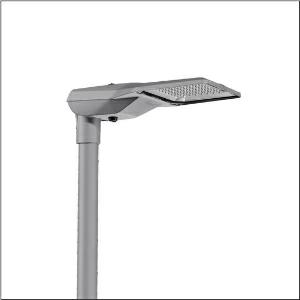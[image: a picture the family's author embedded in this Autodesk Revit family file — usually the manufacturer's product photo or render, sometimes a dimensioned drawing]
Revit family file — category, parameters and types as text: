
# Revit family: streetlight_sl_21_iq_midi___st0_8a_5xe3c31y08mb_7afc
name_source: partatom
category: Lighting Fixtures
units: mm (PartAtom-declared; Revit-internal decimal feet)

## family parameters
Cut with Voids When Loaded = No
Host = Face
Light Source = No
Part Type = Normal
Room Calculation Point = No
Round Connector Dimension = Use Diameter
Shared = No

## types (1)
- --- (1 x LED, 18340 lm, 129.3 W, 3000K)
    Apparent Load = 129 VA
    CIE Flux Codes = 38 75 97 100 100
    Color Rendering = 70
    Color Temperature = 3000K
    Default Elevation = 1800 mm
    Description = Streetlight SL 21 iQ midi, mast luminaire, primary light control with lens, of PMMA, primary optical cover: cover, of toughened safety glass, transparent, light distribution: ST0.8a, light emission: direct distribution, primary light characteristic: asymmetric, installation type: post-top, side-entry, LED, High Power LED, rated luminous flux: 18.340lm, luminous efficacy: 142lm/W, light colour: 730, colour temperature: 3000K, control: presetting dimming logarithmic, Street-Remote, Auto-Match, Temp-Guard, Lumen-Switch, Night-Set, Smart-Wire, Light-Fading, Desk-Remote (wireless, voltage-free reading and setting of iQ features in the workshop via application-optimized NFC function/RFID function), optimised constant luminous flux control (CLO 2.0), mains connection: 230..240V, AC, 50/60Hz, start of lifetime: 129W, end of service life: 142W, reduction: 56W, luminaire housing, of diecast aluminium, powder-coated, Siteco® metallic grey (DB 702S), corrosivity category C5 mid according to DIN EN ISO 12944, please order mast flange separately, inclination adjustable: 0°, 5°, 10°, 15°, sealing non-destructively replaceable, multi-level sealing system, length: 644mm, width: 335mm, height: 110mm, mast flange for spigot size: 42mm (side-entry): 5XC10008XM4, 60/48mm (side-entry/post-top): 5XC10108XM2, 76/60mm (side-entry/post-top): 5XC10108XM1, Smart Interface below and above, protection rating (complete): IP66, insulation class (complete): insulation class II (safety insulation), certification: CE, ENEC, ENEC+, VDE, impact resistance: IK09, permissible operating ambient temperature for outdoor applications: -40..+50°C, standard-compliant lighting for roads and squares, packaging unit: 1 piece

Light Distribution: ST0.8a
    Height = 111 mm
    Lamp = 1 x LED
    Lamp Light Flux = 18340 lm
    Lamp Power = 129.3 W
    Lamp count = 1
    Length = 644 mm
    Luminous efficacy = 142 lm/W
    Manufacturer = Siteco
    ModVariant = No
    Model = 5XE3C31Y08MB
    Number of Poles = 1
    OnlyDefault = Yes
    Power Factor = 1
    Product Name = Streetlight SL 21 iQ midi | ST0.8a
    Product group = mast luminaire | pylon top
    ProductGroupID = 6100
    Protection Class = Protection class II
    Protection Degree = IP 66
    RLX_Detail_Level = 1
    RLX_Emergency_Light_Flux = 0 lm
    RLX_Emergency_Type = 0
    RLX_Emergency_Type_DB = No
    RlxData = <blob elided: 91389 chars, md5=4efca640>
    Socket = socket
    Standby Power = 0 W
    System Light Flux = 18340 lm
    System Power = 129 W
    Type Comments = factory setting: luminous flux: 100 % | dim-lin: 254 | 672 mA
    Type Image = l_1004304.jpg
    URL = http://relux.com
    VarID = @adj_043309
    Voltage = 0 V
    Weight = 0.00 kg
    Width = 336 mm

## geometry (parser evidence)
native form markers: Blend x4, Sweep x11
no freeform markers — native parametric forms only
